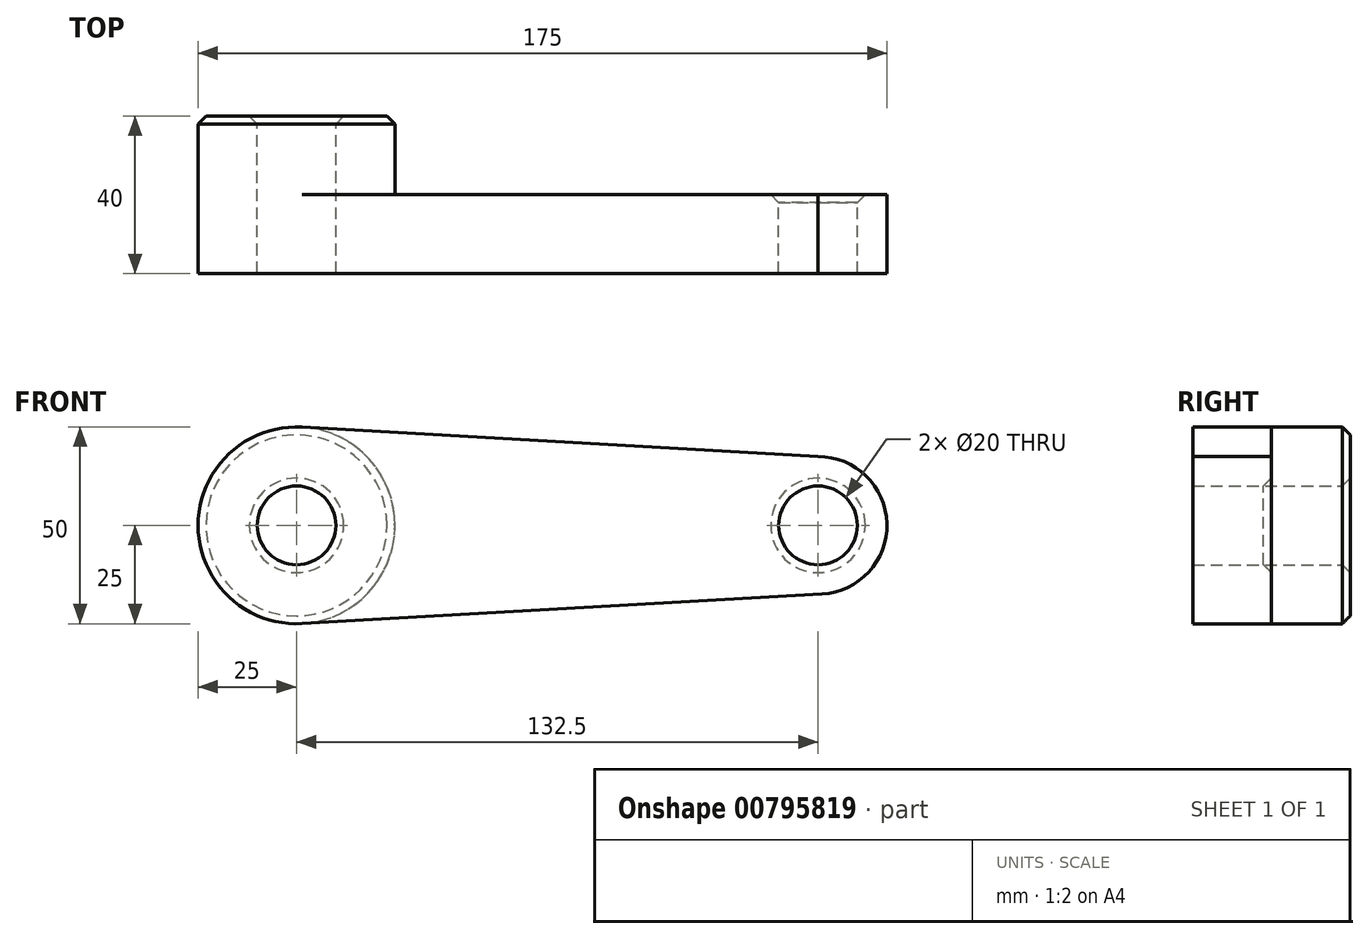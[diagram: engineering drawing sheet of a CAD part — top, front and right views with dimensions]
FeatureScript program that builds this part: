
annotation { "Feature Type Name" : "Feature", "Feature Type Description" : "" }
export const myFeature = defineFeature(function(context is Context, id is Id, definition is map)
    precondition{}
    {
        {
            var Q0;
            Q0=qCreatedBy(makeId("Front.planeOp"),FACE);
            var sketch = newSketch(context, id + "F0", { "sketchPlane" : qUnion([Q0])});
            skCircle(sketch, "E0", {"center": v(0, 0) * mm, "radius": 25 * mm});
            skCircle(sketch, "E1", {"center": v(132.5, 0) * mm, "radius": 17.5 * mm});
            skLineSegment(sketch, "E2", {"start": v(1.42, -24.96) * mm, "end": v(133.5, -17.47) * mm});
            skLineSegment(sketch, "E3", {"start": v(133.5, -17.47) * mm, "end": v(133.5, -17.47) * mm});
            skLineSegment(sketch, "E4", {"start": v(1.42, 24.96) * mm, "end": v(132.5, 17.5) * mm});
            skCircle(sketch, "E5", {"center": v(0, 0) * mm, "radius": 10 * mm});
            skCircle(sketch, "E6", {"center": v(132.5, 0) * mm, "radius": 10 * mm});
            skSolve(sketch);
        }
        {
            var Q0;
            Q0 = qSketchRegion(id + "F0", true);
            extrude(context, id + "F1", {"entities" : qUnion([Q0]), "depth" : 20 * mm, "offsetDistance" : 25 * mm});
        }
        {
            var Q0;
            Q0=makeQuery(id+"F0.imprint","IMPRINT",FACE,{"disambiguationData":[TD([[makeQuery(id+"F0.imprint","IMPRINT",EDGE,{"derivedFrom":sQuery(id+"F0.wireOp",EDGE,"E5")}),-1.0]])]});
            extrude(context, id + "F2", {"entities" : qUnion([Q0]), "operationType" : NewBodyOperationType.ADD, "oppositeDirection" : true, "depth" : 20 * mm, "offsetDistance" : 25 * mm});
        }
        {
            var Q0;
            Q0=makeQuery(id+"F2.opExtrude","CAP_EDGE",EDGE,{"disambiguationData":[OSD([sQuery(id+"F0.wireOp",EDGE,"E5")])],"isStart":false});
            var Q1;
            Q1=makeQuery(id+"F2.opExtrude","CAP_EDGE",EDGE,{"disambiguationData":[OSD([sQuery(id+"F0.wireOp",EDGE,"E0")])],"isStart":false});
            var Q2;
            Q2=makeQuery(id+"F1.opExtrude","CAP_EDGE",EDGE,{"disambiguationData":[OSD([sQuery(id+"F0.wireOp",EDGE,"E6")])],"isStart":true});
            chamfer(context, id + "F3", {"entities" : qUnion([Q0, Q1, Q2]), "width" : 2 * mm, "tangentPropagation" : true});
        }
    });
